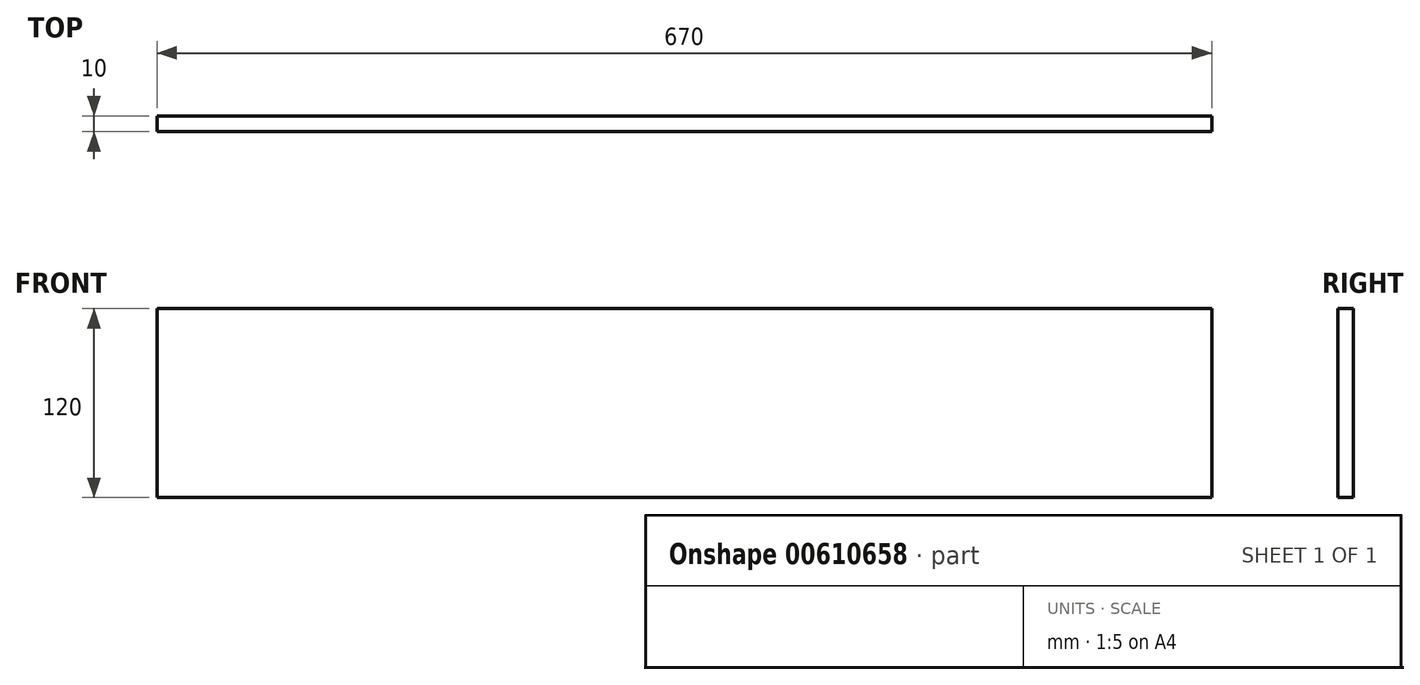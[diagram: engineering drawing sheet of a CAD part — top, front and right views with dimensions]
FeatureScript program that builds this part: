
annotation { "Feature Type Name" : "Feature", "Feature Type Description" : "" }
export const myFeature = defineFeature(function(context is Context, id is Id, definition is map)
    precondition{}
    {
        {
            var Q0;
            Q0=qCreatedBy(makeId("Front.planeOp"),FACE);
            var sketch = newSketch(context, id + "F0", { "sketchPlane" : qUnion([Q0])});
            skLineSegment(sketch, "E0.bottom", {"start": v(-279.26, -109.92) * mm, "end": v(390.74, -109.92) * mm});
            skLineSegment(sketch, "E0.top", {"start": v(-279.26, -229.92) * mm, "end": v(390.74, -229.92) * mm});
            skLineSegment(sketch, "E0.left", {"start": v(-279.26, -109.92) * mm, "end": v(-279.26, -229.92) * mm});
            skLineSegment(sketch, "E0.right", {"start": v(390.74, -109.92) * mm, "end": v(390.74, -229.92) * mm});
            skPoint(sketch, "E1.endSnap0", {"position": v(55.74, -109.92) * mm});
            skSolve(sketch);
        }
        {
            var Q0;
            Q0=makeQuery(id+"F0.imprint","IMPRINT",FACE,{"disambiguationData":[TD([[makeQuery(id+"F0.imprint","IMPRINT",EDGE,{"derivedFrom":sQuery(id+"F0.wireOp",EDGE,"E0.bottom")}),-1.0]])]});
            extrude(context, id + "F1", {"entities" : qUnion([Q0]), "depth" : 10 * mm, "offsetDistance" : 25 * mm});
        }
    });
